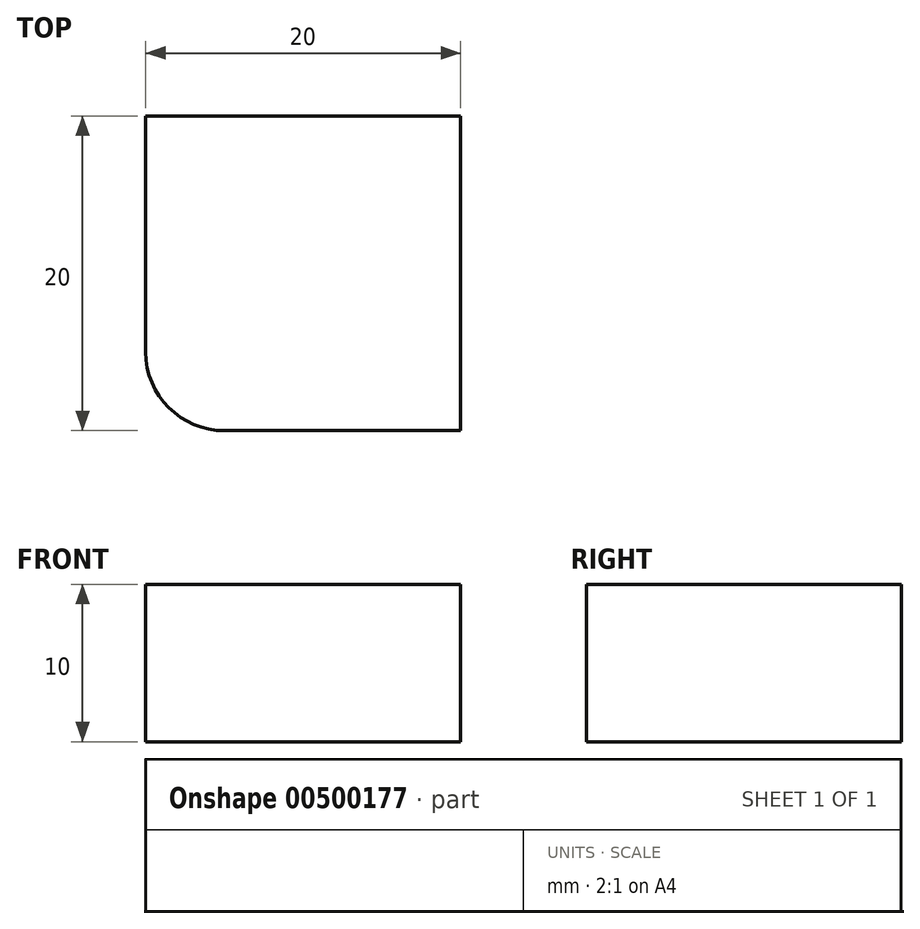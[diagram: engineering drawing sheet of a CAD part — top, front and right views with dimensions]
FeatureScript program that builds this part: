
annotation { "Feature Type Name" : "Feature", "Feature Type Description" : "" }
export const myFeature = defineFeature(function(context is Context, id is Id, definition is map)
    precondition{}
    {
        {
            var Q0;
            Q0=qCreatedBy(makeId("Top.planeOp"),FACE);
            var sketch = newSketch(context, id + "F0", { "sketchPlane" : qUnion([Q0])});
            skLineSegment(sketch, "E0.bottom", {"start": v(0, 0) * mm, "end": v(20, 0) * mm});
            skLineSegment(sketch, "E0.top", {"start": v(0, 20) * mm, "end": v(20, 20) * mm});
            skLineSegment(sketch, "E0.left", {"start": v(0, 0) * mm, "end": v(0, 20) * mm});
            skLineSegment(sketch, "E0.right", {"start": v(20, 0) * mm, "end": v(20, 20) * mm});
            skSolve(sketch);
        }
        {
            var Q0;
            Q0=makeQuery(id+"F0.imprint","IMPRINT",FACE,{"disambiguationData":[TD([[makeQuery(id+"F0.imprint","IMPRINT",EDGE,{"derivedFrom":sQuery(id+"F0.wireOp",EDGE,"E0.bottom")}),1.0]])]});
            var sketch = newSketch(context, id + "F1", { "sketchPlane" : qUnion([Q0])});
            skSolve(sketch);
        }
        {
            var Q0;
            Q0 = qSketchRegion(id + "F1", true);
            var Q1;
            Q1=makeQuery(id+"F0.imprint","IMPRINT",FACE,{"disambiguationData":[TD([[makeQuery(id+"F0.imprint","IMPRINT",EDGE,{"derivedFrom":sQuery(id+"F0.wireOp",EDGE,"E0.bottom")}),1.0]])]});
            extrude(context, id + "F2", {"entities" : qUnion([Q0, Q1]), "depth" : 10 * mm});
        }
        {
            var Q0;
            Q0=makeQuery(id+"F2.opExtrude","SWEPT_EDGE",EDGE,{"disambiguationData":[OSD([sQuery(id+"F0.wireOp",EDGE,"E0.bottom"),sQuery(id+"F0.wireOp",EDGE,"E0.left")])]});
            fillet(context, id + "F3", {"entities" : qUnion([Q0]), "radius" : 5 * mm, "tangentPropagation" : true, "allowEdgeOverflow" : false});
        }
    });
